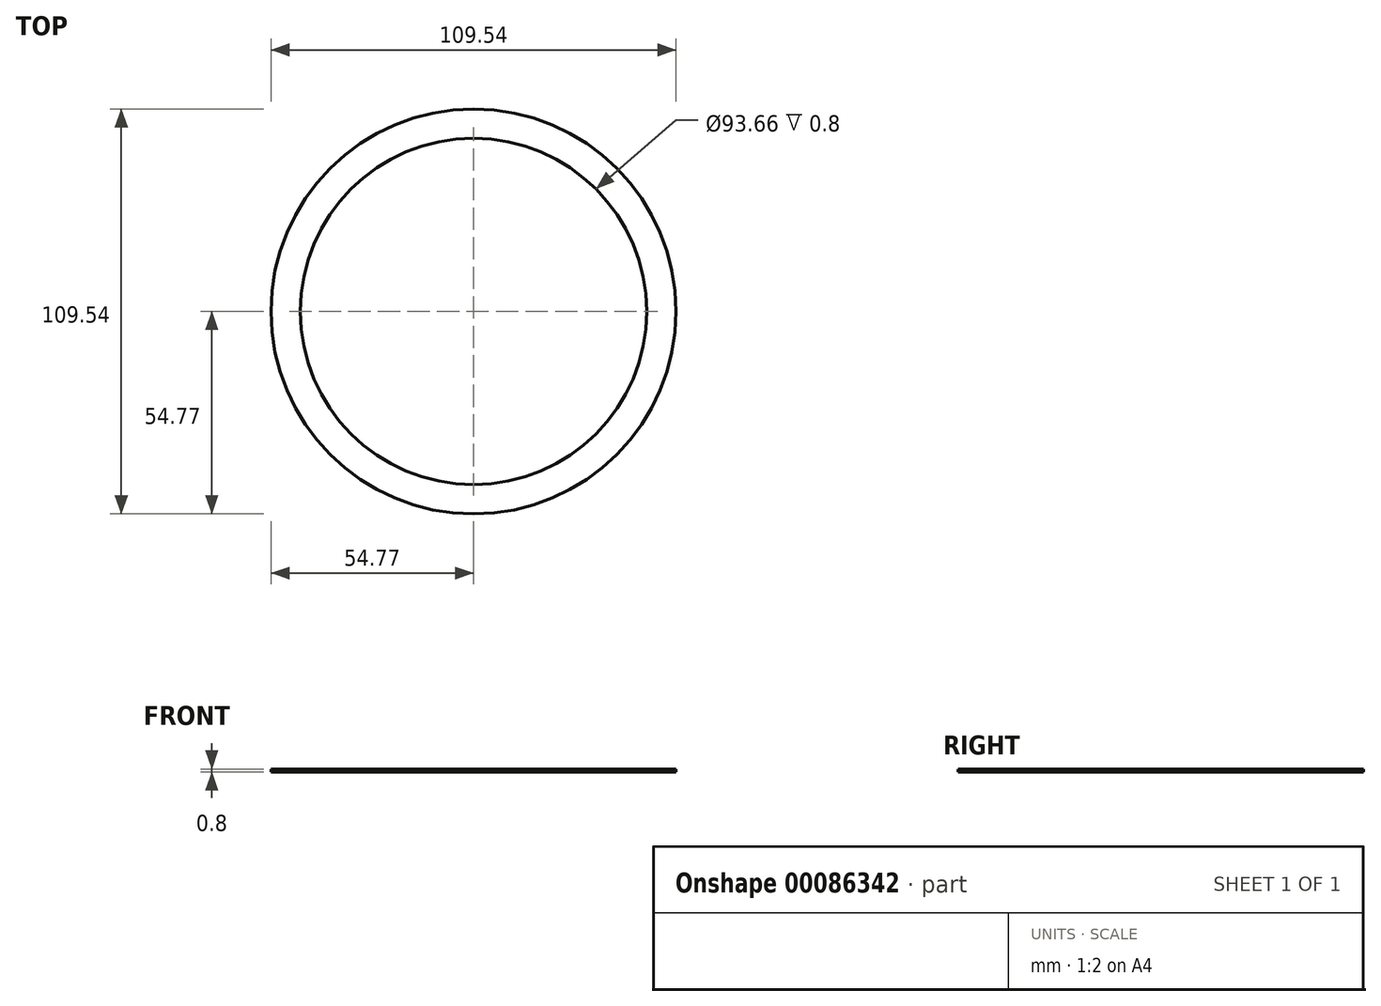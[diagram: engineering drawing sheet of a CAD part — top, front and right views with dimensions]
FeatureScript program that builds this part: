
annotation { "Feature Type Name" : "Feature", "Feature Type Description" : "" }
export const myFeature = defineFeature(function(context is Context, id is Id, definition is map)
    precondition{}
    {
        {
            var Q0;
            Q0=qCreatedBy(makeId("Front.planeOp"),FACE);
            var sketch = newSketch(context, id + "F0", { "sketchPlane" : qUnion([Q0])});
            skLineSegment(sketch, "E0.bottom", {"start": v(46.83, 0) * mm, "end": v(54.77, 0) * mm});
            skLineSegment(sketch, "E0.top", {"start": v(46.83, 0.8) * mm, "end": v(54.77, 0.8) * mm});
            skLineSegment(sketch, "E0.left", {"start": v(46.83, 0) * mm, "end": v(46.83, 0.8) * mm});
            skLineSegment(sketch, "E0.right", {"start": v(54.77, 0) * mm, "end": v(54.77, 0.8) * mm});
            skLineSegment(sketch, "E1", {"start": v(0, 9.36) * mm, "end": v(0, -26.9) * mm, "construction": true});
            skSolve(sketch);
        }
        {
            var Q0;
            Q0 = qSketchRegion(id + "F0", true);
            var Q1;
            Q1=sQuery(id+"F0.wireOp",EDGE,"E1");
            revolve(context, id + "F1", {"surfaceOperationType" : NewSurfaceOperationType.NEW, "entities" : qUnion([Q0]), "axis" : qUnion([Q1]), "revolveType" : RevolveType.FULL});
        }
    });
